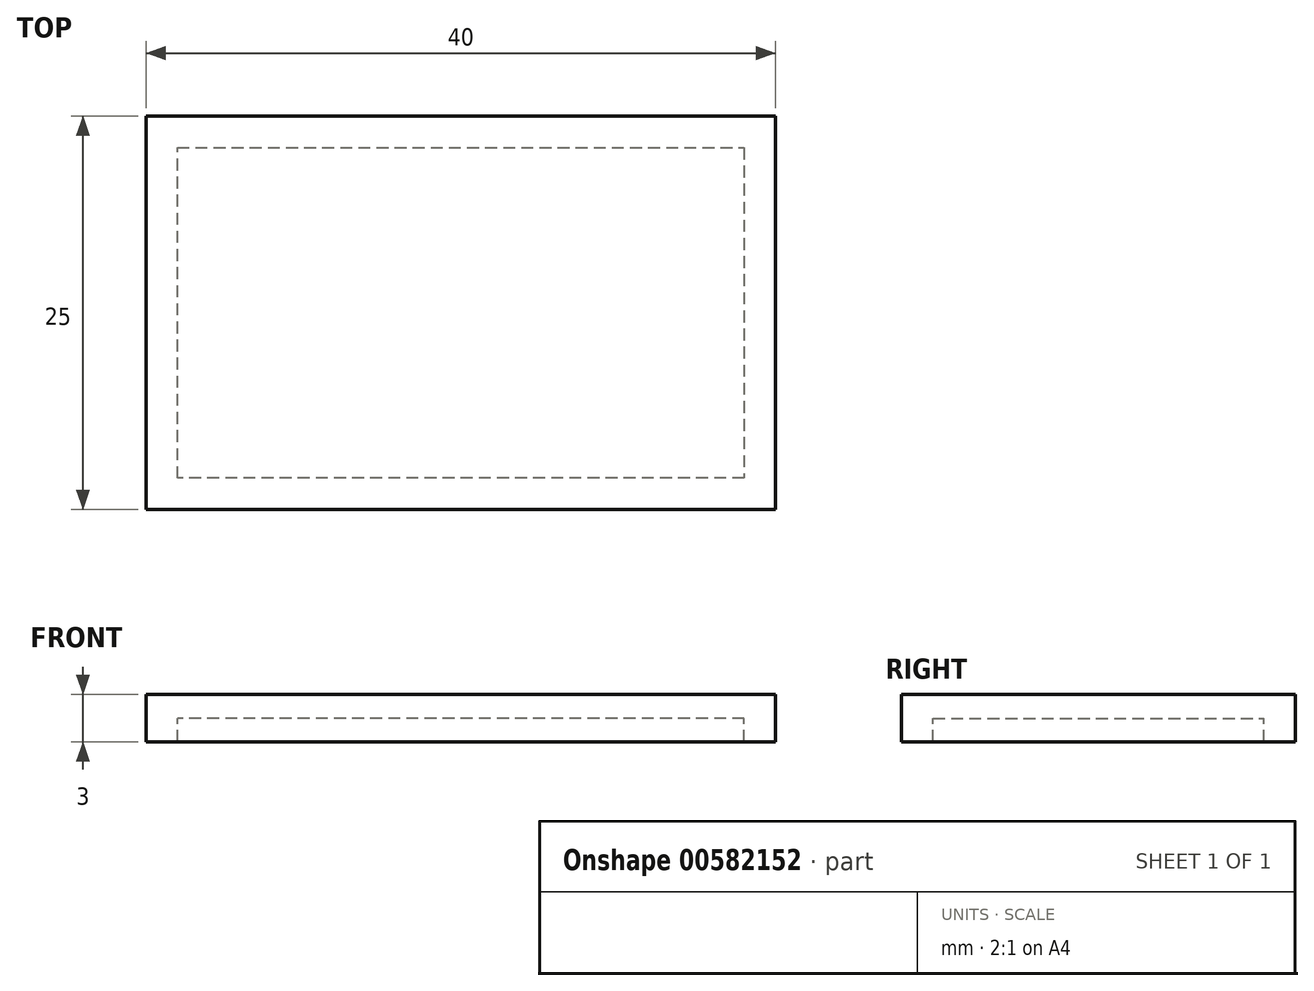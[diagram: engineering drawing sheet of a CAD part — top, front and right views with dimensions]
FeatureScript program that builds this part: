
annotation { "Feature Type Name" : "Feature", "Feature Type Description" : "" }
export const myFeature = defineFeature(function(context is Context, id is Id, definition is map)
    precondition{}
    {
        {
            var Q0;
            Q0=qCreatedBy(makeId("Top.planeOp"),FACE);
            var sketch = newSketch(context, id + "F0", { "sketchPlane" : qUnion([Q0])});
            skLineSegment(sketch, "E0.bottom", {"start": v(-20, 12.5) * mm, "end": v(20, 12.5) * mm});
            skLineSegment(sketch, "E0.top", {"start": v(-20, -12.5) * mm, "end": v(20, -12.5) * mm});
            skLineSegment(sketch, "E0.left", {"start": v(-20, 12.5) * mm, "end": v(-20, -12.5) * mm});
            skLineSegment(sketch, "E0.right", {"start": v(20, 12.5) * mm, "end": v(20, -12.5) * mm});
            skPoint(sketch, "E0.middle", {"position": v(0, 0) * mm});
            skSolve(sketch);
        }
        {
            var Q0;
            Q0=sQuery(id+"F0.wireOp",EDGE,"E0.bottom");
            var Q1;
            Q1=sQuery(id+"F0.wireOp",EDGE,"E0.right");
            var Q2;
            Q2=sQuery(id+"F0.wireOp",EDGE,"E0.top");
            var Q3;
            Q3=sQuery(id+"F0.wireOp",EDGE,"E0.left");
            extrude(context, id + "F1", {"bodyType" : ToolBodyType.SURFACE, "surfaceEntities" : qUnion([Q0, Q1, Q2, Q3]), "depth" : 1.5 * mm, "offsetDistance" : 25.4 * mm});
        }
        {
            var Q0;
            Q0 = qSketchRegion(id + "F0", true);
            extrude(context, id + "F2", {"entities" : qUnion([Q0]), "depth" : 1.5 * mm, "offsetDistance" : 25.4 * mm});
        }
        {
            var Q0;
            Q0=makeQuery(id+"F2.opExtrude","CAP_FACE",FACE,{"disambiguationData":[OSD([sQuery(id+"F0.wireOp",EDGE,"E0.bottom"),sQuery(id+"F0.wireOp",EDGE,"E0.top"),sQuery(id+"F0.wireOp",EDGE,"E0.left"),sQuery(id+"F0.wireOp",EDGE,"E0.right")])],"isStart":true});
            var sketch = newSketch(context, id + "F3", { "sketchPlane" : qUnion([Q0])});
            skLineSegment(sketch, "E1.bottom", {"start": v(-20, -12.5) * mm, "end": v(20, -12.5) * mm});
            skLineSegment(sketch, "E1.top", {"start": v(-20, 12.5) * mm, "end": v(20, 12.5) * mm});
            skLineSegment(sketch, "E1.left", {"start": v(-20, -12.5) * mm, "end": v(-20, 12.5) * mm});
            skLineSegment(sketch, "E1.right", {"start": v(20, -12.5) * mm, "end": v(20, 12.5) * mm});
            skLineSegment(sketch, "E2.0", {"start": v(-18, 10.5) * mm, "end": v(-18, -10.5) * mm});
            skLineSegment(sketch, "E2.1", {"start": v(18, 10.5) * mm, "end": v(-18, 10.5) * mm});
            skLineSegment(sketch, "E2.2", {"start": v(18, -10.5) * mm, "end": v(18, 10.5) * mm});
            skLineSegment(sketch, "E2.3", {"start": v(-18, -10.5) * mm, "end": v(18, -10.5) * mm});
            skSolve(sketch);
        }
        {
            var Q0;
            Q0 = qSketchRegion(id + "F3", true);
            extrude(context, id + "F4", {"entities" : qUnion([Q0]), "operationType" : NewBodyOperationType.ADD, "depth" : 1.5 * mm, "offsetDistance" : 25.4 * mm});
        }
        {
            var Q0;
            Q0=makeQuery(id+"F2.opExtrude","CAP_FACE",FACE,{"disambiguationData":[OSD([sQuery(id+"F0.wireOp",EDGE,"E0.bottom"),sQuery(id+"F0.wireOp",EDGE,"E0.top"),sQuery(id+"F0.wireOp",EDGE,"E0.left"),sQuery(id+"F0.wireOp",EDGE,"E0.right")])],"isStart":true});
            var sketch = newSketch(context, id + "F5", { "sketchPlane" : qUnion([Q0])});
            skText(sketch, "E3", { "text": "子堯", "fontName": "OpenSans-Regular.ttf"});
            skPoint(sketch, "E4", {"position": v(18, 0.24) * mm});
            skPoint(sketch, "E5", {"position": v(8.58, 0.24) * mm});
            skText(sketch, "E6", { "text": "子堯", "fontName": "NotoSansCJKtc-Regular.otf"});
            skCircle(sketch, "E7", {"center": v(-3.34, 8.38) * mm, "radius": 2.9 * mm});
            const initialGuessF5  = {"E3": [-0.02342, -0.00913, 1, 0, 0.01874], "E6": [-0.02129, -0.00786, 1, 0, 0.01454]};
            skSetInitialGuess(sketch, initialGuessF5);
            skSolve(sketch);
        }
        {
            var Q0;
            Q0=sQuery(id+"F5.wireOp",EDGE,"E7");
            extrude(context, id + "F6", {"bodyType" : ToolBodyType.SURFACE, "surfaceEntities" : qUnion([Q0]), "depth" : 25.4 * mm, "offsetDistance" : 25.4 * mm});
        }
    });
